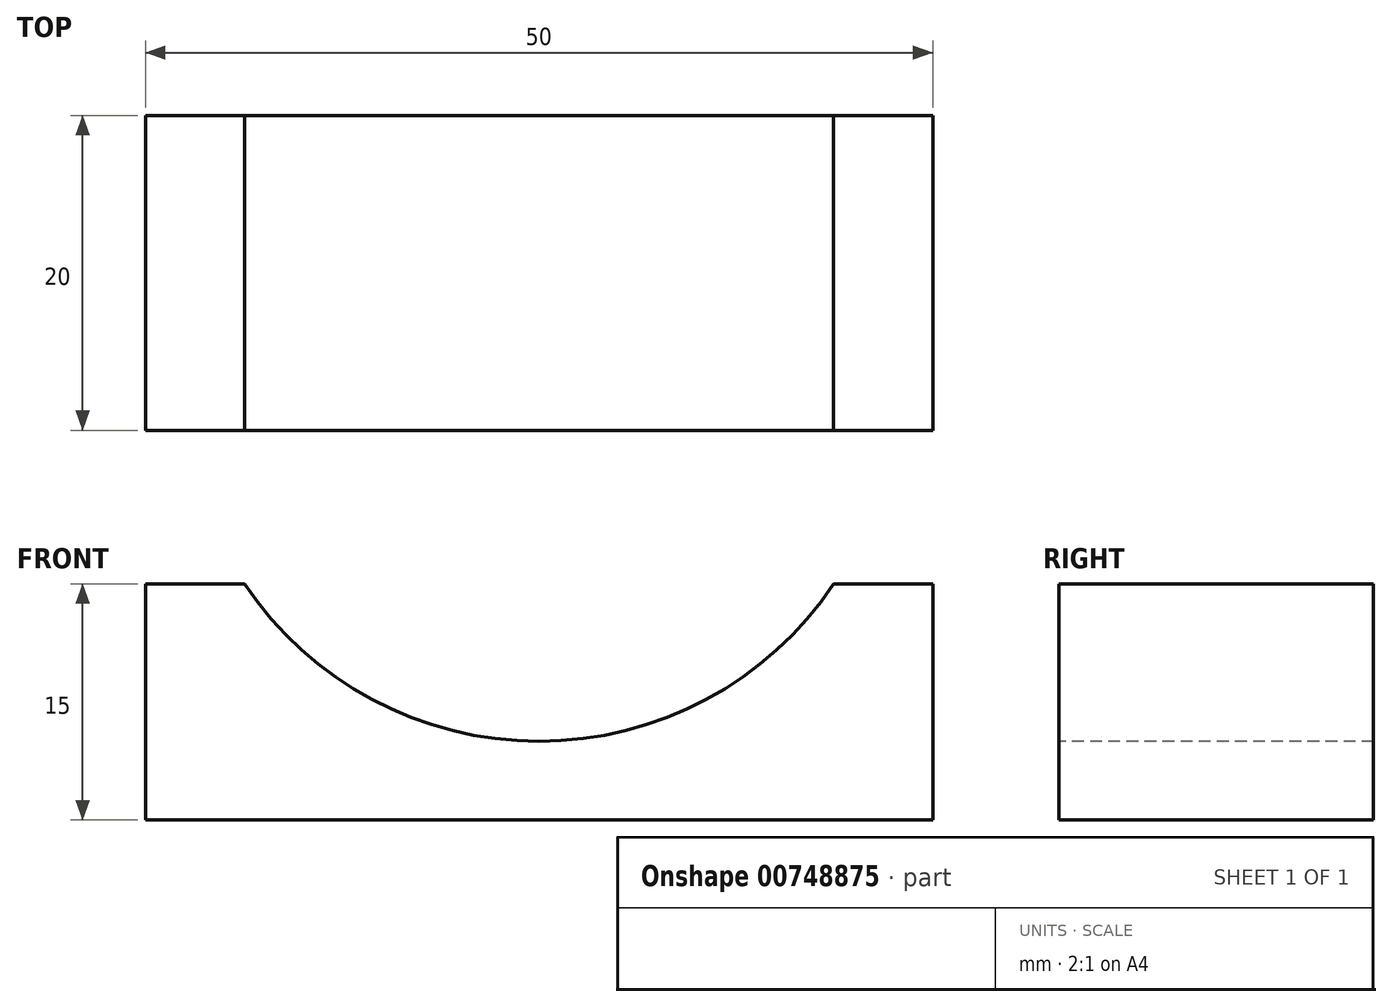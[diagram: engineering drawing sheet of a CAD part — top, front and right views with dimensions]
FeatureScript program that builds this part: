
annotation { "Feature Type Name" : "Feature", "Feature Type Description" : "" }
export const myFeature = defineFeature(function(context is Context, id is Id, definition is map)
    precondition{}
    {
        {
            var Q0;
            Q0=qCreatedBy(makeId("Top.planeOp"),FACE);
            var sketch = newSketch(context, id + "F0", { "sketchPlane" : qUnion([Q0])});
            skLineSegment(sketch, "E0.bottom", {"start": v(-25, -10) * mm, "end": v(25, -10) * mm});
            skLineSegment(sketch, "E0.top", {"start": v(-25, 10) * mm, "end": v(25, 10) * mm});
            skLineSegment(sketch, "E0.left", {"start": v(-25, -10) * mm, "end": v(-25, 10) * mm});
            skLineSegment(sketch, "E0.right", {"start": v(25, -10) * mm, "end": v(25, 10) * mm});
            skPoint(sketch, "E0.middle", {"position": v(0, 0) * mm});
            skSolve(sketch);
        }
        {
            var Q0;
            Q0 = qSketchRegion(id + "F0", true);
            extrude(context, id + "F1", {"entities" : qUnion([Q0]), "depth" : 20 * mm, "offsetDistance" : 25 * mm});
        }
        {
            var Q0;
            Q0=makeQuery(id+"F1.opExtrude","SWEPT_FACE",FACE,{"disambiguationData":[OSD([sQuery(id+"F0.wireOp",EDGE,"E0.bottom")])]});
            var sketch = newSketch(context, id + "F2", { "sketchPlane" : qUnion([Q0])});
            skCircle(sketch, "E1", {"center": v(0, 32.5) * mm, "radius": 22.5 * mm});
            skSolve(sketch);
        }
        {
            var Q0;
            Q0 = qSketchRegion(id + "F2", true);
            extrude(context, id + "F3", {"entities" : qUnion([Q0]), "operationType" : NewBodyOperationType.REMOVE, "oppositeDirection" : true, "depth" : 25 * mm, "offsetDistance" : 25 * mm});
        }
        {
            var Q0;
            Q0=makeQuery(id+"F1.opExtrude","SWEPT_FACE",FACE,{"disambiguationData":[OSD([sQuery(id+"F0.wireOp",EDGE,"E0.bottom")])]});
            var sketch = newSketch(context, id + "F4", { "sketchPlane" : qUnion([Q0])});
            skLineSegment(sketch, "E2.bottom", {"start": v(-25, 0) * mm, "end": v(25, 0) * mm});
            skLineSegment(sketch, "E2.top", {"start": v(-25, 5) * mm, "end": v(25, 5) * mm});
            skLineSegment(sketch, "E2.left", {"start": v(-25, 0) * mm, "end": v(-25, 5) * mm});
            skLineSegment(sketch, "E2.right", {"start": v(25, 0) * mm, "end": v(25, 5) * mm});
            skSolve(sketch);
        }
        {
            var Q0;
            Q0 = qSketchRegion(id + "F4", true);
            extrude(context, id + "F5", {"entities" : qUnion([Q0]), "operationType" : NewBodyOperationType.REMOVE, "oppositeDirection" : true, "depth" : 25 * mm, "offsetDistance" : 25 * mm});
        }
    });
